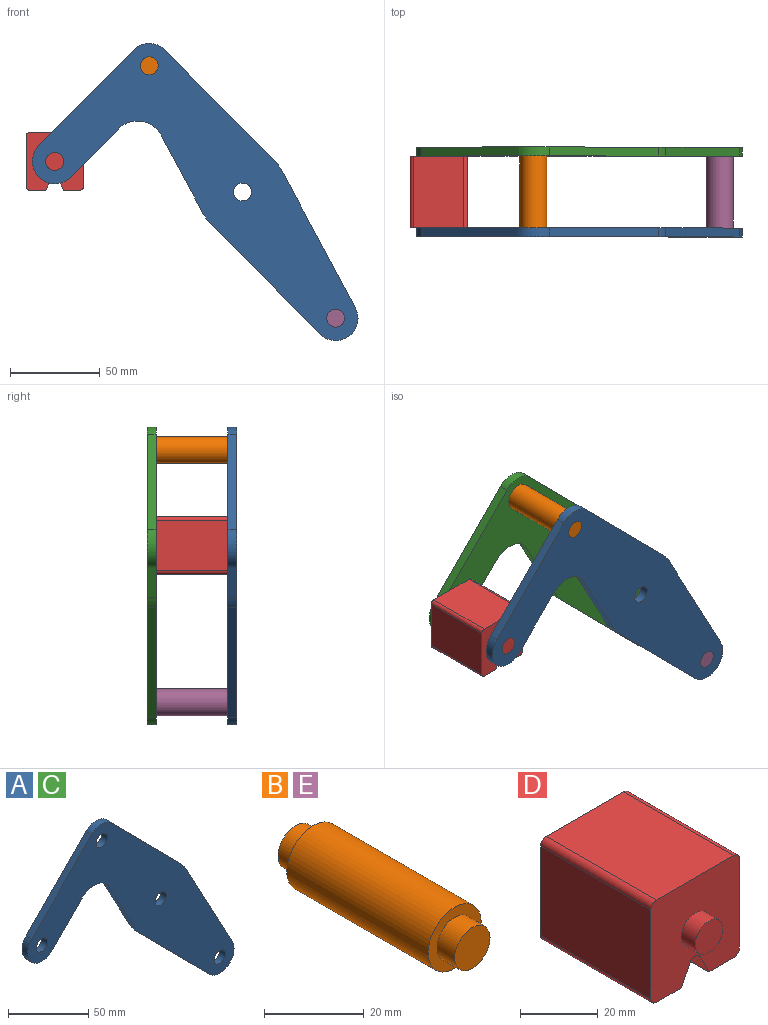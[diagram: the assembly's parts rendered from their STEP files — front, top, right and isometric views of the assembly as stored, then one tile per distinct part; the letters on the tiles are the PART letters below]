
ASSEMBLY  parts=5 mates=3
PART A: 18 faces, bbox 181.7x5x165.8 mm
  f0: plane 43.49x23.35mm, normal (-0.88,0,-0.47), area 246.8mm2, adj f1,f14,f16,f17
  f1: cylinder r=25mm len=5.75mm, axis (0,1,0), area 35.8mm2, adj f0,f2,f16,f17
  f2: plane 61.6x60.87mm, normal (-0.71,0,-0.7), area 433mm2, adj f1,f3,f16,f17
  f3: cylinder r=12.5mm len=21.39mm, axis (0,1,0), area 178.4mm2, adj f2,f4,f16,f17
  f4: plane 76.3x40.96mm, normal (0.88,0,0.47), area 433mm2, adj f3,f5,f16,f17
  f5: cylinder r=25mm len=5.75mm, axis (0,1,0), area 35.8mm2, adj f4,f6,f16,f17
  f6: plane 61.6x60.87mm, normal (0.71,0,0.7), area 433mm2, adj f5,f7,f16,f17
  f7: cylinder r=12.5mm len=17.78mm, axis (0,1,0), area 98.9mm2, adj f6,f8,f16,f17
  f8: plane 53.35x52.71mm, normal (-0.71,0,0.7), area 375mm2, adj f7,f9,f16,f17
  f9: cylinder r=12.5mm len=21.39mm, axis (0,1,0), area 196.3mm2, adj f8,f10,f16,f17
  f10: plane 26.86x26.54mm, normal (0.71,0,-0.7), area 188.8mm2, adj f9,f14,f16,f17
  f11: cylinder r=5mm len=10mm, axis (0,1,0), area 157.1mm2, adj f16,f17
  f12: cylinder r=5mm len=10mm, axis (0,1,0), area 157.1mm2, adj f16,f17
  f13: cylinder r=5mm len=10mm, axis (0,1,0), area 157.1mm2, adj f16,f17
  f14: cylinder r=15mm len=23.89mm, axis (0,1,0), area 140.2mm2, adj f0,f10,f16,f17
  f15: cylinder r=5mm len=10mm, axis (0,1,0), area 157.1mm2, adj f16,f17
  f16: plane 181.66x165.78mm, normal (0,-1,0), area 8710.1mm2, adj f0,f1,f2,f3,f4,f5,f6,f7
  f17: plane 181.66x165.78mm, normal (0,1,0), area 8710.1mm2, adj f0,f1,f2,f3,f4,f5,f6,f7
PART B: 7 faces, bbox 15x50x15 mm
  f0: cylinder r=7.5mm len=40mm, axis (0,-1,0), area 1885mm2, adj f2,f5
  f1: cylinder r=5mm len=10mm, axis (0,1,0), area 157.1mm2, adj f2,f3
  f2: plane 15x15mm, normal (0,-1,0), area 98.2mm2, adj f0,f1
  f3: plane 10x10mm, normal (0,-1,0), area 78.5mm2, adj f1
  f4: cylinder r=5mm len=10mm, axis (0,-1,0), area 157.1mm2, adj f5,f6
  f5: plane 15x15mm, normal (0,1,0), area 98.2mm2, adj f0,f4
  f6: plane 10x10mm, normal (0,1,0), area 78.5mm2, adj f4
PART C: same geometry as A
PART D: 18 faces, bbox 32.1x50x32.1 mm
  f0: plane 40x28.08mm, normal (1,0,0), area 1123.1mm2, adj f4,f10,f13,f14
  f1: plane 40x9.04mm, normal (0,0,-1), area 361.6mm2, adj f2,f4,f10,f14
  f2: plane 40x6.42mm, normal (-0.89,0,-0.45), area 287.2mm2, adj f1,f4,f10,f15
  f3: plane 40x6.42mm, normal (0.89,0,-0.45), area 287.2mm2, adj f4,f5,f10,f15
  f4: plane 32.08x32.08mm, normal (0,-1,0), area 900.6mm2, adj f0,f1,f2,f3,f5,f6,f7,f9
  f5: plane 40x9.04mm, normal (0,0,-1), area 361.6mm2, adj f3,f4,f10,f16
  f6: plane 40x28.08mm, normal (0,0,1), area 1123.1mm2, adj f4,f10,f13,f17
  f7: plane 40x28.08mm, normal (-1,0,0), area 1123.1mm2, adj f4,f10,f16,f17
  f8: plane 10x10mm, normal (0,-1,0), area 78.5mm2, adj f9
  f9: cylinder r=5mm len=10mm, axis (0,1,0), area 157.1mm2, adj f4,f8
  f10: plane 32.08x32.08mm, normal (0,1,0), area 900.6mm2, adj f0,f1,f2,f3,f5,f6,f7,f12
  f11: plane 10x10mm, normal (0,1,0), area 78.5mm2, adj f12
  f12: cylinder r=5mm len=10mm, axis (0,-1,0), area 157.1mm2, adj f10,f11
  f13: cylinder r=2mm len=40mm, axis (0,1,0), area 125.7mm2, adj f0,f4,f6,f10
  f14: cylinder r=2mm len=40mm, axis (0,-1,0), area 125.7mm2, adj f0,f1,f4,f10
  f15: cylinder r=2mm len=40mm, axis (0,1,0), area 177.1mm2, adj f2,f3,f4,f10
  f16: cylinder r=2mm len=40mm, axis (0,1,0), area 125.7mm2, adj f4,f5,f7,f10
  f17: cylinder r=2mm len=40mm, axis (0,-1,0), area 125.7mm2, adj f4,f6,f7,f10
PART E: same geometry as B
PLACE A t=(0,-20,0)mm fixed
PLACE B t=(0,-20,0)mm
PLACE C t=(0,25,0)mm
PLACE D t=(0,-20,0)mm
PLACE E t=(103.95,-20,-140.78)mm
MATE fastened C.f7 <-> B.f0  axis (0,-1,0) through (-51.98,20,70.39)mm
MATE fastened E.f0 <-> A.f3  axis (0,-1,0) through (51.98,-20,-70.39)mm
MATE revolute D.f9 <-> A.f9  axis (0,-1,0) through (-104.69,-20,17.04)mm
